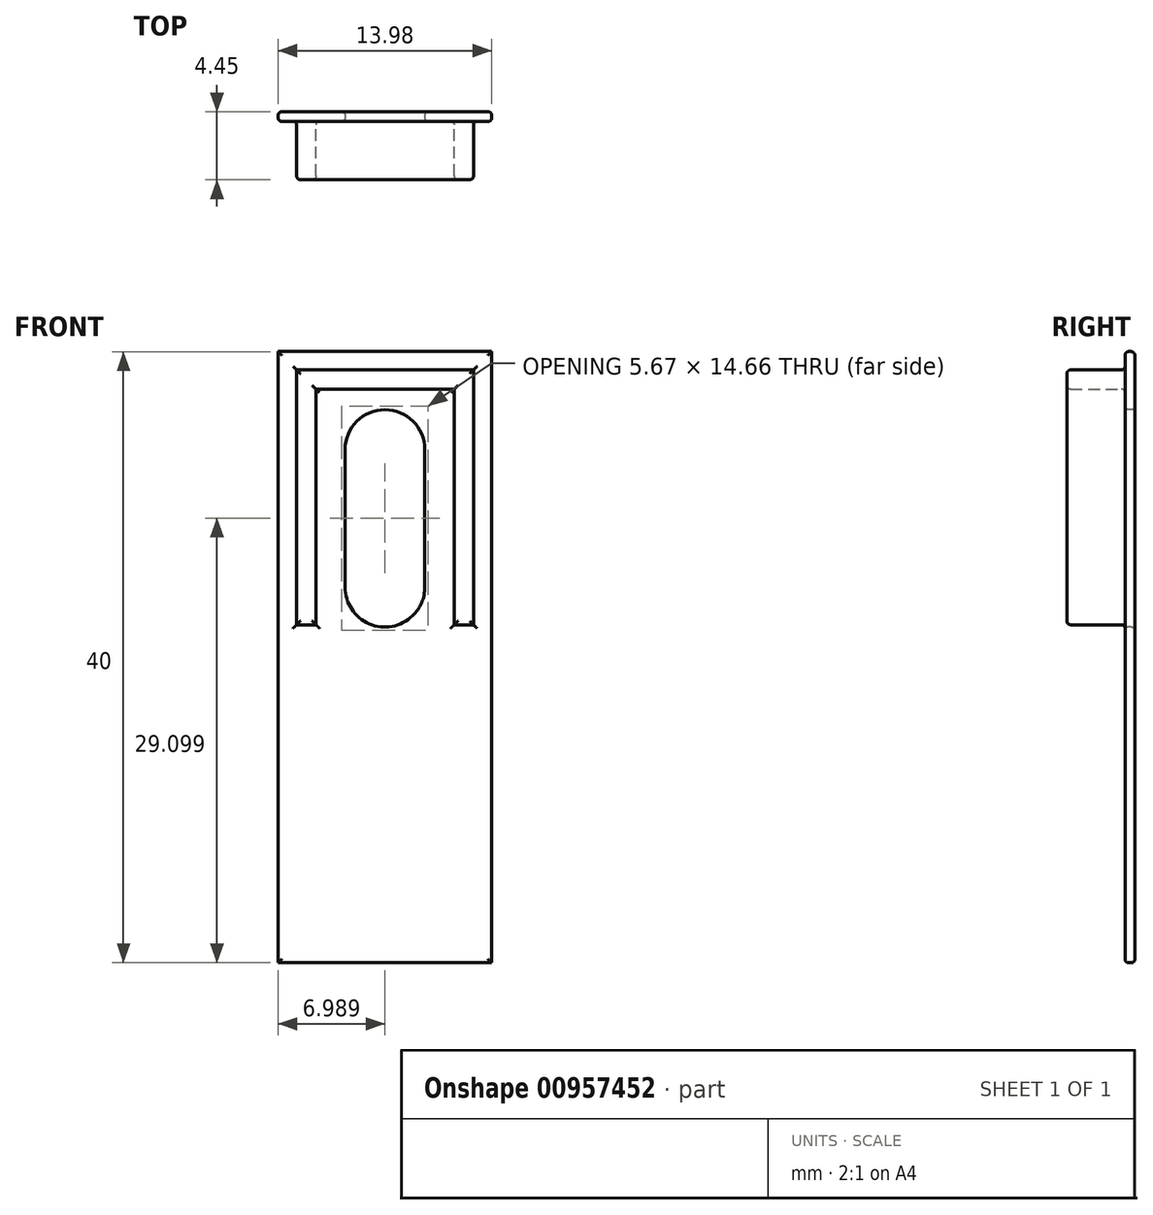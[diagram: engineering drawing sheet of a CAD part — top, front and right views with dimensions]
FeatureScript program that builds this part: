
annotation { "Feature Type Name" : "Feature", "Feature Type Description" : "" }
export const myFeature = defineFeature(function(context is Context, id is Id, definition is map)
    precondition{}
    {
        {
            var Q0;
            Q0=qCreatedBy(makeId("Front.planeOp"),FACE);
            var sketch = newSketch(context, id + "F0", { "sketchPlane" : qUnion([Q0])});
            skLineSegment(sketch, "E0.bottom", {"start": v(6.99, 20) * mm, "end": v(-6.98, 20) * mm});
            skLineSegment(sketch, "E0.top", {"start": v(6.98, -20) * mm, "end": v(-6.99, -20) * mm});
            skPoint(sketch, "E0.middle", {"position": v(0, 0) * mm});
            skLineSegment(sketch, "E1", {"start": v(6.99, 20) * mm, "end": v(6.98, -20) * mm});
            skLineSegment(sketch, "E2", {"start": v(-6.98, 20) * mm, "end": v(-6.99, -20) * mm});
            skSolve(sketch);
        }
        {
            var Q0;
            Q0=makeQuery(id+"F0.imprint","IMPRINT",FACE,{"disambiguationData":[TD([[makeQuery(id+"F0.imprint","IMPRINT",EDGE,{"derivedFrom":sQuery(id+"F0.wireOp",EDGE,"E0.bottom")}),1.0]])]});
            extrude(context, id + "F1", {"entities" : qUnion([Q0]), "depth" : 3.17 * mm, "offsetDistance" : 25.4 * mm});
        }
        {
            var Q0;
            Q0=makeQuery(id+"F1.opExtrude","CAP_FACE",FACE,{"disambiguationData":[OSD([sQuery(id+"F0.wireOp",EDGE,"E0.bottom"),sQuery(id+"F0.wireOp",EDGE,"E0.top"),sQuery(id+"F0.wireOp",EDGE,"E1"),sQuery(id+"F0.wireOp",EDGE,"E2")])],"isStart":true});
            extrude(context, id + "F2", {"entities" : qUnion([Q0]), "operationType" : NewBodyOperationType.REMOVE, "oppositeDirection" : true, "depth" : 2.54 * mm, "offsetDistance" : 25.4 * mm});
        }
        {
            var Q0;
            Q0=makeQuery(id+"F1.opExtrude","CAP_FACE",FACE,{"disambiguationData":[OSD([sQuery(id+"F0.wireOp",EDGE,"E0.bottom"),sQuery(id+"F0.wireOp",EDGE,"E0.top"),sQuery(id+"F0.wireOp",EDGE,"E1"),sQuery(id+"F0.wireOp",EDGE,"E2")])],"isStart":false});
            var sketch = newSketch(context, id + "F3", { "sketchPlane" : qUnion([Q0])});
            skArc(sketch, "E3.0", {"start": v(2.6, 13.6) * mm, "mid": v(1.84, 15.44) * mm, "end": v(0, 16.2) * mm});
            skLineSegment(sketch, "E3.1", {"start": v(-2.6, 13.6) * mm, "end": v(-2.6, 4.59) * mm});
            skArc(sketch, "E3.2", {"start": v(-2.6, 4.59) * mm, "mid": v(-1.02, 2.19) * mm, "end": v(1.8, 2.7) * mm});
            skArc(sketch, "E3.3", {"start": v(0, 16.2) * mm, "mid": v(-1.84, 15.44) * mm, "end": v(-2.6, 13.6) * mm});
            skArc(sketch, "E3.4", {"start": v(1.8, 2.7) * mm, "mid": v(2.4, 3.56) * mm, "end": v(2.6, 4.58) * mm});
            skLineSegment(sketch, "E3.5", {"start": v(2.6, 4.58) * mm, "end": v(2.6, 13.6) * mm});
            skLineSegment(sketch, "E4", {"start": v(0, 1.98) * mm, "end": v(0, 16.2) * mm});
            skSolve(sketch);
        }
        {
            var Q0;
            Q0=makeQuery(id+"F1.opExtrude","CAP_FACE",FACE,{"disambiguationData":[OSD([sQuery(id+"F0.wireOp",EDGE,"E0.bottom"),sQuery(id+"F0.wireOp",EDGE,"E0.top"),sQuery(id+"F0.wireOp",EDGE,"E1"),sQuery(id+"F0.wireOp",EDGE,"E2")])],"isStart":false});
            var sketch = newSketch(context, id + "F4", { "sketchPlane" : qUnion([Q0])});
            skPoint(sketch, "E5.middle", {"position": v(0, 10.1) * mm});
            skLineSegment(sketch, "E6", {"start": v(-4.51, 2.12) * mm, "end": v(-4.51, 17.54) * mm});
            skLineSegment(sketch, "E7.MirrorCS", {"start": v(4.53, 2.12) * mm, "end": v(4.53, 17.54) * mm});
            skLineSegment(sketch, "E8", {"start": v(-4.51, 17.54) * mm, "end": v(4.53, 17.54) * mm});
            skLineSegment(sketch, "E9", {"start": v(4.53, 2.12) * mm, "end": v(5.8, 2.12) * mm});
            skLineSegment(sketch, "E10", {"start": v(5.8, 2.12) * mm, "end": v(5.8, 18.8) * mm});
            skLineSegment(sketch, "E11", {"start": v(-4.51, 2.12) * mm, "end": v(-5.78, 2.12) * mm});
            skLineSegment(sketch, "E12", {"start": v(5.8, 18.8) * mm, "end": v(-5.78, 18.8) * mm});
            skLineSegment(sketch, "E13", {"start": v(-5.78, 18.8) * mm, "end": v(-5.78, 2.12) * mm});
            skSolve(sketch);
        }
        {
            var Q0;
            Q0=makeQuery(id+"F3.imprint","IMPRINT",FACE,{"disambiguationData":[TD([[makeQuery(id+"F3.imprint","IMPRINT",EDGE,{"derivedFrom":sQuery(id+"F3.wireOp",EDGE,"E3.0")}),1.0]])]});
            var Q1;
            {var subQ0=sQuery(id+"F3.wireOp",EDGE,"E3.1");Q1=makeQuery(id+"F3.imprint","IMPRINT",FACE,{"disambiguationData":[TD([[makeQuery(id+"F3.imprint","IMPRINT",EDGE,{"derivedFrom":subQ0}),1.0]])]});}
            extrude(context, id + "F5", {"entities" : qUnion([Q0, Q1]), "operationType" : NewBodyOperationType.REMOVE, "oppositeDirection" : true, "depth" : 25.4 * mm, "offsetDistance" : 25.4 * mm});
        }
        {
            var Q0;
            Q0=makeQuery(id+"F4.imprint","IMPRINT",FACE,{"disambiguationData":[TD([[makeQuery(id+"F4.imprint","IMPRINT",EDGE,{"derivedFrom":sQuery(id+"F4.wireOp",EDGE,"E6")}),1.0]])]});
            extrude(context, id + "F6", {"entities" : qUnion([Q0]), "operationType" : NewBodyOperationType.ADD, "depth" : 3.8 * mm, "offsetDistance" : 25.4 * mm});
        }
        {
            var Q0;
            Q0=makeQuery(id+"F2.boolean.opBoolean","COPY",FACE,{"derivedFrom":makeQuery(id+"F2.opExtrude","CAP_FACE",FACE,{"disambiguationData":[OSD([sQuery(id+"F0.wireOp",EDGE,"E0.bottom"),sQuery(id+"F0.wireOp",EDGE,"E0.top"),sQuery(id+"F0.wireOp",EDGE,"E1"),sQuery(id+"F0.wireOp",EDGE,"E2")])],"isStart":false})});
            fillet(context, id + "F7", {"entities" : qUnion([Q0]), "radius" : 0.23 * mm, "tangentPropagation" : true, "allowEdgeOverflow" : false});
        }
        {
            var Q0;
            Q0=makeQuery(id+"F1.opExtrude","CAP_FACE",FACE,{"disambiguationData":[OSD([sQuery(id+"F0.wireOp",EDGE,"E0.bottom"),sQuery(id+"F0.wireOp",EDGE,"E0.top"),sQuery(id+"F0.wireOp",EDGE,"E1"),sQuery(id+"F0.wireOp",EDGE,"E2")])],"isStart":false});
            fillet(context, id + "F8", {"entities" : qUnion([Q0]), "radius" : 0.23 * mm, "tangentPropagation" : true, "allowEdgeOverflow" : false});
        }
        {
            var Q0;
            Q0=makeQuery(id+"F6.opExtrude","CAP_FACE",FACE,{"disambiguationData":[OSD([sQuery(id+"F4.wireOp",EDGE,"E6"),sQuery(id+"F4.wireOp",EDGE,"E7.MirrorCS"),sQuery(id+"F4.wireOp",EDGE,"E8"),sQuery(id+"F4.wireOp",EDGE,"E9"),sQuery(id+"F4.wireOp",EDGE,"E10"),sQuery(id+"F4.wireOp",EDGE,"E11"),sQuery(id+"F4.wireOp",EDGE,"E12"),sQuery(id+"F4.wireOp",EDGE,"E13")])],"isStart":false});
            fillet(context, id + "F9", {"entities" : qUnion([Q0]), "radius" : 0.25 * mm, "tangentPropagation" : true, "allowEdgeOverflow" : false});
        }
    });
